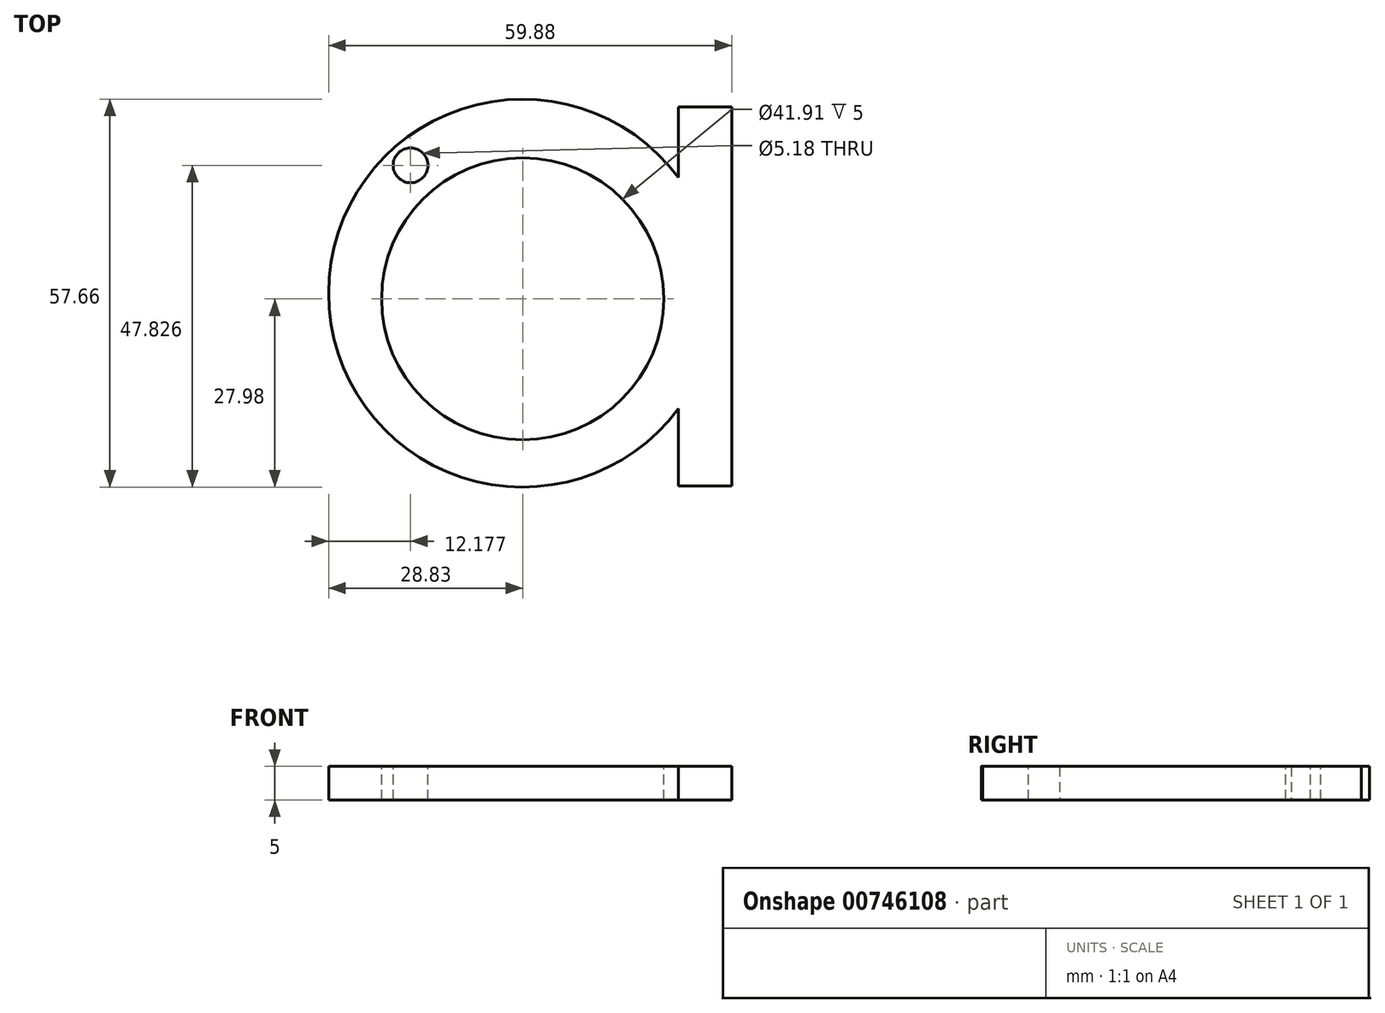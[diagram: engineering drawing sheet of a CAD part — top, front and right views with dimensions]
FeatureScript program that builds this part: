
annotation { "Feature Type Name" : "Feature", "Feature Type Description" : "" }
export const myFeature = defineFeature(function(context is Context, id is Id, definition is map)
    precondition{}
    {
        {
            var Q0;
            Q0=qCreatedBy(makeId("Top.planeOp"),FACE);
            var sketch = newSketch(context, id + "F0", { "sketchPlane" : qUnion([Q0])});
            skCircle(sketch, "E0", {"center": v(0, 0.85) * mm, "radius": 28.83 * mm});
            skSolve(sketch);
        }
        {
            var Q0;
            Q0=makeQuery(id+"F0.imprint","IMPRINT",FACE,{"disambiguationData":[TD([[makeQuery(id+"F0.imprint","IMPRINT",EDGE,{"derivedFrom":sQuery(id+"F0.wireOp",EDGE,"E0")}),1.0]])]});
            extrude(context, id + "F1", {"entities" : qUnion([Q0]), "depth" : 5 * mm, "offsetDistance" : 25.4 * mm});
        }
        {
            var Q0;
            Q0=makeQuery(id+"F1.opExtrude","CAP_FACE",FACE,{"disambiguationData":[OSD([sQuery(id+"F0.wireOp",EDGE,"E0")])],"isStart":false});
            var sketch = newSketch(context, id + "F2", { "sketchPlane" : qUnion([Q0])});
            skCircle(sketch, "E1", {"center": v(0, 0) * mm, "radius": 20.96 * mm});
            skSolve(sketch);
        }
        {
            var Q0;
            Q0=makeQuery(id+"F2.imprint","IMPRINT",FACE,{"disambiguationData":[TD([[makeQuery(id+"F2.imprint","IMPRINT",EDGE,{"derivedFrom":sQuery(id+"F2.wireOp",EDGE,"E1")}),1.0]])]});
            extrude(context, id + "F3", {"entities" : qUnion([Q0]), "operationType" : NewBodyOperationType.REMOVE, "oppositeDirection" : true, "depth" : 5 * mm, "offsetDistance" : 25.4 * mm});
        }
        {
            var Q0;
            Q0=qCreatedBy(makeId("Top.planeOp"),FACE);
            var sketch = newSketch(context, id + "F4", { "sketchPlane" : qUnion([Q0])});
            skLineSegment(sketch, "E2.bottom", {"start": v(23.14, 28.5) * mm, "end": v(31.05, 28.5) * mm});
            skLineSegment(sketch, "E2.top", {"start": v(23.14, -27.8) * mm, "end": v(31.05, -27.8) * mm});
            skLineSegment(sketch, "E2.left", {"start": v(23.14, 28.5) * mm, "end": v(23.14, -27.8) * mm});
            skLineSegment(sketch, "E2.right", {"start": v(31.05, 28.5) * mm, "end": v(31.05, -27.8) * mm});
            skSolve(sketch);
        }
        {
            var Q0;
            Q0=makeQuery(id+"F4.imprint","IMPRINT",FACE,{"disambiguationData":[TD([[makeQuery(id+"F4.imprint","IMPRINT",EDGE,{"derivedFrom":sQuery(id+"F4.wireOp",EDGE,"E2.bottom")}),-1.0]])]});
            extrude(context, id + "F5", {"entities" : qUnion([Q0]), "operationType" : NewBodyOperationType.ADD, "depth" : 5 * mm, "offsetDistance" : 25.4 * mm});
        }
        {
            var Q0;
            Q0=makeQuery(id+"F5.boolean.opBoolean","MERGE",FACE,{"derivedFrom":[makeQuery(id+"F1.opExtrude","CAP_FACE",FACE,{"disambiguationData":[OSD([sQuery(id+"F0.wireOp",EDGE,"E0")])],"isStart":false}),makeQuery(id+"F5.opExtrude","CAP_FACE",FACE,{"disambiguationData":[OSD([sQuery(id+"F4.wireOp",EDGE,"E2.bottom"),sQuery(id+"F4.wireOp",EDGE,"E2.top"),sQuery(id+"F4.wireOp",EDGE,"E2.left"),sQuery(id+"F4.wireOp",EDGE,"E2.right")])],"isStart":false})]});
            var sketch = newSketch(context, id + "F6", { "sketchPlane" : qUnion([Q0])});
            skCircle(sketch, "E3", {"center": v(0, 25.9) * mm, "radius": 2.6 * mm});
            skCircle(sketch, "E4.1.0", {"center": v(-22.44, -12.95) * mm, "radius": 2.6 * mm});
            skCircle(sketch, "E4.2.0", {"center": v(22.44, -12.95) * mm, "radius": 2.6 * mm});
            skPoint(sketch, "E4.center", {"position": v(0, 0) * mm});
            skCircle(sketch, "E5.1.0", {"center": v(-16.65, 19.85) * mm, "radius": 2.6 * mm});
            skCircle(sketch, "E5.2.0", {"center": v(-25.51, 4.5) * mm, "radius": 2.6 * mm});
            skCircle(sketch, "E5.4.0", {"center": v(-8.86, -24.34) * mm, "radius": 2.6 * mm});
            skCircle(sketch, "E6.1.5.0", {"center": v(8.86, -24.34) * mm, "radius": 2.6 * mm});
            skCircle(sketch, "E6.1.7.0", {"center": v(25.51, 4.5) * mm, "radius": 2.6 * mm});
            skCircle(sketch, "E6.1.8.0", {"center": v(16.65, 19.85) * mm, "radius": 2.6 * mm});
            skSolve(sketch);
        }
        {
            var Q0;
            Q0=makeQuery(id+"F6.imprint","IMPRINT",FACE,{"disambiguationData":[TD([[makeQuery(id+"F6.imprint","IMPRINT",EDGE,{"derivedFrom":sQuery(id+"F6.wireOp",EDGE,"E5.1.0")}),1.0]])]});
            extrude(context, id + "F7", {"entities" : qUnion([Q0]), "operationType" : NewBodyOperationType.REMOVE, "oppositeDirection" : true, "depth" : 5 * mm, "offsetDistance" : 25.4 * mm});
        }
    });
